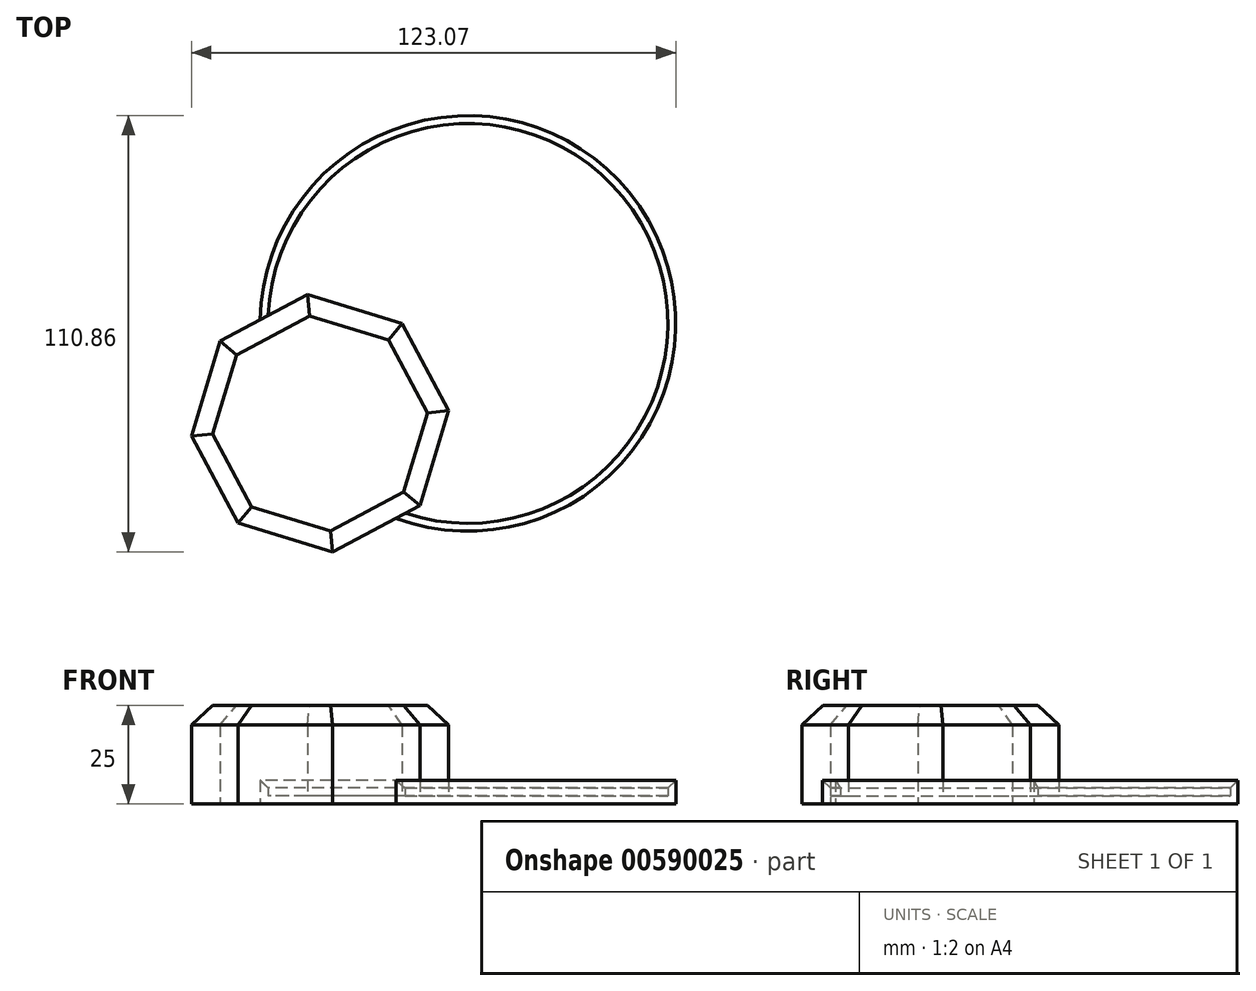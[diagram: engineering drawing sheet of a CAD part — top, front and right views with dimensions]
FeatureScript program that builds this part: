
annotation { "Feature Type Name" : "Feature", "Feature Type Description" : "" }
export const myFeature = defineFeature(function(context is Context, id is Id, definition is map)
    precondition{}
    {
        {
            var Q0;
            Q0=qCreatedBy(makeId("Top.planeOp"),FACE);
            var sketch = newSketch(context, id + "F0", { "sketchPlane" : qUnion([Q0])});
            skCircle(sketch, "E0", {"center": v(0, 0) * mm, "radius": 52.79 * mm});
            skSolve(sketch);
        }
        {
            var Q0;
            Q0=makeQuery(id+"F0.imprint","IMPRINT",FACE,{"disambiguationData":[TD([[makeQuery(id+"F0.imprint","IMPRINT",EDGE,{"derivedFrom":sQuery(id+"F0.wireOp",EDGE,"E0")}),1.0]])]});
            extrude(context, id + "F1", {"entities" : qUnion([Q0]), "depth" : 9 * mm, "offsetDistance" : 25.4 * mm});
        }
        {
            var Q0;
            Q0=makeQuery(id+"F1.opExtrude","CAP_FACE",FACE,{"disambiguationData":[OSD([sQuery(id+"F0.wireOp",EDGE,"E0")])],"isStart":false});
            shell(context, id + "F2", {"entities" : qUnion([Q0]), "thickness" : 2 * mm});
        }
        {
            var Q0;
            Q0=qCreatedBy(makeId("Top.planeOp"),FACE);
            var sketch = newSketch(context, id + "F3", { "sketchPlane" : qUnion([Q0])});
            skCircle(sketch, "E1.cCircle", {"center": v(-37.59, -25.38) * mm, "radius": 32.85 * mm, "construction": true});
            skLineSegment(sketch, "E1.0", {"start": v(-16.74, 0) * mm, "end": v(-4.9, -22.18) * mm});
            skLineSegment(sketch, "E1.1", {"start": v(-4.9, -22.18) * mm, "end": v(-12.2, -46.23) * mm});
            skLineSegment(sketch, "E1.2", {"start": v(-12.2, -46.23) * mm, "end": v(-34.38, -58.07) * mm});
            skLineSegment(sketch, "E1.3", {"start": v(-34.38, -58.07) * mm, "end": v(-58.44, -50.76) * mm});
            skLineSegment(sketch, "E1.4", {"start": v(-58.44, -50.76) * mm, "end": v(-70.28, -28.58) * mm});
            skLineSegment(sketch, "E1.5", {"start": v(-70.28, -28.58) * mm, "end": v(-62.97, -4.53) * mm});
            skLineSegment(sketch, "E1.6", {"start": v(-62.97, -4.53) * mm, "end": v(-40.8, 7.3) * mm});
            skLineSegment(sketch, "E1.7", {"start": v(-40.8, 7.3) * mm, "end": v(-16.74, 0) * mm});
            skSolve(sketch);
        }
        {
            var Q0;
            Q0=makeQuery(id+"F3.imprint","IMPRINT",FACE,{"disambiguationData":[TD([[makeQuery(id+"F3.imprint","IMPRINT",EDGE,{"derivedFrom":sQuery(id+"F3.wireOp",EDGE,"E1.0")}),-1.0]])]});
            extrude(context, id + "F4", {"entities" : qUnion([Q0]), "operationType" : NewBodyOperationType.ADD, "depth" : 25 * mm, "offsetDistance" : 25 * mm});
        }
        {
            var Q0;
            Q0=makeQuery(id+"F4.opExtrude","CAP_EDGE",EDGE,{"disambiguationData":[OSD([sQuery(id+"F3.wireOp",EDGE,"E1.3")])],"isStart":false});
            var Q1;
            Q1=makeQuery(id+"F4.opExtrude","CAP_EDGE",EDGE,{"disambiguationData":[OSD([sQuery(id+"F3.wireOp",EDGE,"E1.4")])],"isStart":false});
            var Q2;
            Q2=makeQuery(id+"F4.opExtrude","CAP_EDGE",EDGE,{"disambiguationData":[OSD([sQuery(id+"F3.wireOp",EDGE,"E1.5")])],"isStart":false});
            var Q3;
            {var subQ0=sQuery(id+"F0.wireOp",EDGE,"E0");Q3=makeQuery(id+"F2.opShell","OFFSET_EDGE",EDGE,{"disambiguationData":[OSD([subQ0]),TDD([makeQuery(id+"F1.opExtrude","CAP_EDGE",EDGE,{"disambiguationData":[OSD([subQ0])],"isStart":false})])]});}
            var Q4;
            Q4=makeQuery(id+"F4.opExtrude","CAP_EDGE",EDGE,{"disambiguationData":[OSD([sQuery(id+"F3.wireOp",EDGE,"E1.6")])],"isStart":false});
            var Q5;
            Q5=makeQuery(id+"F4.opExtrude","CAP_EDGE",EDGE,{"disambiguationData":[OSD([sQuery(id+"F3.wireOp",EDGE,"E1.7")])],"isStart":false});
            var Q6;
            Q6=makeQuery(id+"F4.opExtrude","CAP_EDGE",EDGE,{"disambiguationData":[OSD([sQuery(id+"F3.wireOp",EDGE,"E1.0")])],"isStart":false});
            var Q7;
            Q7=makeQuery(id+"F4.opExtrude","CAP_FACE",FACE,{"disambiguationData":[OSD([sQuery(id+"F3.wireOp",EDGE,"E1.0"),sQuery(id+"F3.wireOp",EDGE,"E1.1"),sQuery(id+"F3.wireOp",EDGE,"E1.2"),sQuery(id+"F3.wireOp",EDGE,"E1.3"),sQuery(id+"F3.wireOp",EDGE,"E1.4"),sQuery(id+"F3.wireOp",EDGE,"E1.5"),sQuery(id+"F3.wireOp",EDGE,"E1.6"),sQuery(id+"F3.wireOp",EDGE,"E1.7")])],"isStart":false});
            chamfer(context, id + "F5", {"entities" : qUnion([Q0, Q1, Q2, Q3, Q4, Q5, Q6, Q7]), "width" : 5 * mm, "tangentPropagation" : true});
        }
    });
